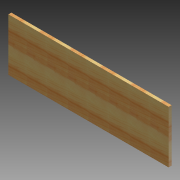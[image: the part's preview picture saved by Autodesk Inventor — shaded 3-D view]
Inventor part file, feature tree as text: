
AUTODESK INVENTOR PART (.ipt)
format: ipt  version: 2012 (Build 160160000, 160)  size: 87,552 bytes
history: native  units: in
note: dims shown in document units (in); Inventor stores cm internally (conversion verified against a paired STEP export)
features: extrude x1, sketch x1
ambient origin geometry x8: Origin, YZ Plane, XZ Plane, XY Plane, X Axis, Y Axis, Z Axis, Center Point
bodies: Solid1 (feature_tree)
feature tree (2):
  extrude  "Extrusion1"  Depth=9.0in
  sketch  "Sketch1"  dims[d0=27.5in d1=9.0in d2=0.5in d3=0.0in]
